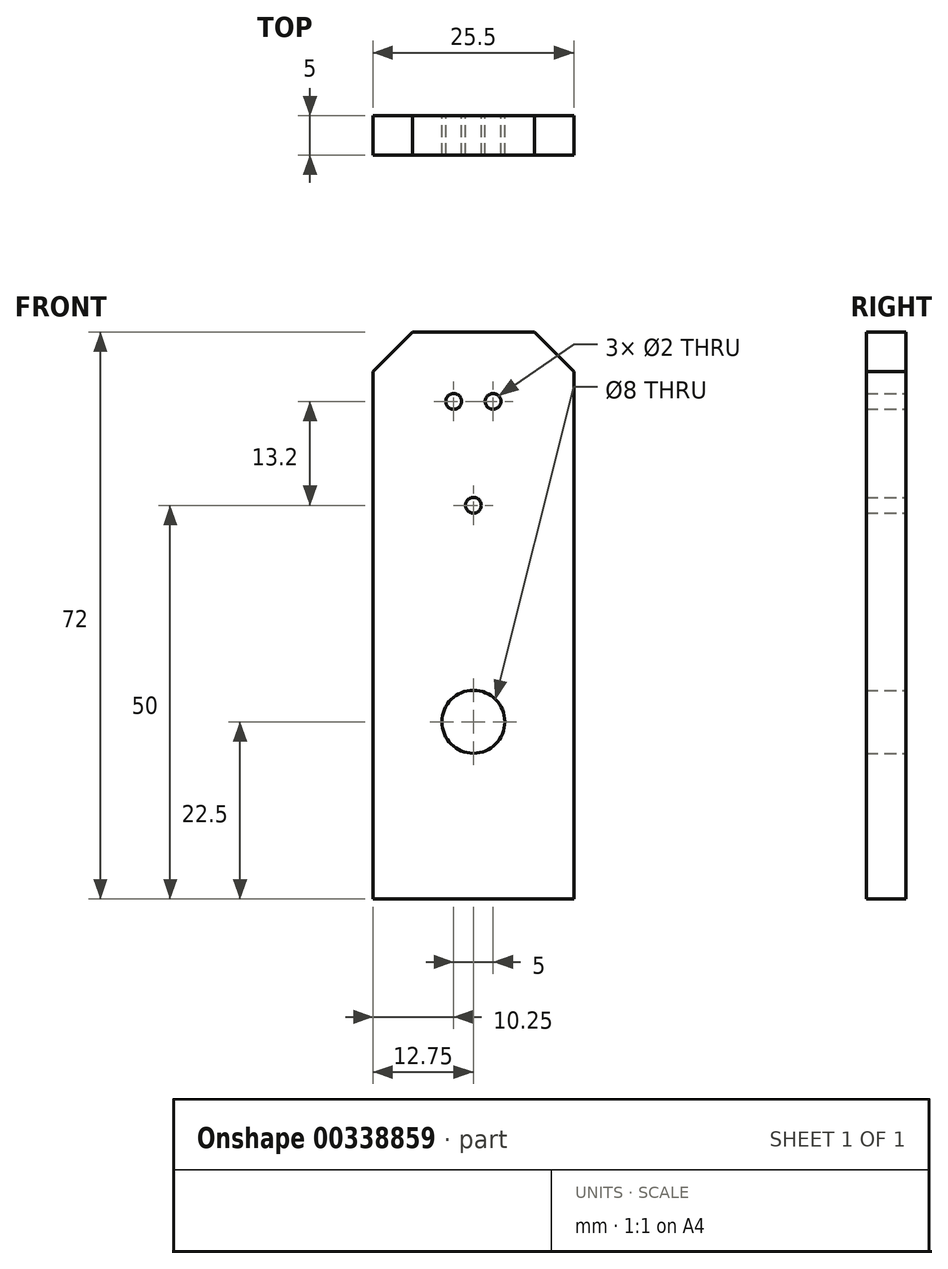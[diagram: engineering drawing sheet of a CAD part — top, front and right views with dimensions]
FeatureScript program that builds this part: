
annotation { "Feature Type Name" : "Feature", "Feature Type Description" : "" }
export const myFeature = defineFeature(function(context is Context, id is Id, definition is map)
    precondition{}
    {
        {
            var Q0;
            Q0=qCreatedBy(makeId("Front.planeOp"),FACE);
            var sketch = newSketch(context, id + "F0", { "sketchPlane" : qUnion([Q0])});
            skLineSegment(sketch, "E0.bottom", {"start": v(0, 0) * mm, "end": v(25.5, 0) * mm});
            skLineSegment(sketch, "E0.top", {"start": v(5, 72) * mm, "end": v(20.5, 72) * mm});
            skLineSegment(sketch, "E0.left", {"start": v(0, 0) * mm, "end": v(0, 67) * mm});
            skLineSegment(sketch, "E0.right", {"start": v(25.5, 0) * mm, "end": v(25.5, 67) * mm});
            skLineSegment(sketch, "E1", {"start": v(5, 72) * mm, "end": v(0, 67) * mm});
            skLineSegment(sketch, "E2", {"start": v(20.5, 72) * mm, "end": v(25.5, 67) * mm});
            skPoint(sketch, "E3", {"position": v(12.75, 22.5) * mm});
            skCircle(sketch, "E4", {"center": v(12.75, 22.5) * mm, "radius": 4 * mm});
            skCircle(sketch, "E5", {"center": v(12.75, 50) * mm, "radius": 1 * mm});
            skCircle(sketch, "E6", {"center": v(10.25, 63.2) * mm, "radius": 1 * mm});
            skCircle(sketch, "E7", {"center": v(15.25, 63.2) * mm, "radius": 1 * mm});
            skSolve(sketch);
        }
        {
            var Q0;
            Q0=makeQuery(id+"F0.imprint","IMPRINT",FACE,{"disambiguationData":[TD([[makeQuery(id+"F0.imprint","IMPRINT",EDGE,{"derivedFrom":sQuery(id+"F0.wireOp",EDGE,"E0.bottom")}),1.0]])]});
            extrude(context, id + "F1", {"entities" : qUnion([Q0]), "depth" : 5 * mm});
        }
    });
